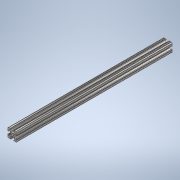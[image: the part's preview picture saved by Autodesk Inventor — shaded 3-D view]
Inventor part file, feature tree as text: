
AUTODESK INVENTOR PART (.ipt)
format: ipt  version: 2020 (Build 240168000, 168)  size: 239,104 bytes
history: native  units: in
note: dims shown in document units (in); Inventor stores cm internally (conversion verified against a paired STEP export)
features: extrude x1, sketch x1
ambient origin geometry x8: Origin, YZ Plane, XZ Plane, XY Plane, X Axis, Y Axis, Z Axis, Center Point
bodies: Solid1 (feature_tree)
feature tree (2):
  extrude  "Extrusion1"  [1 undecoded]
  sketch  "Sketch1"  dims[d0=17.0in d1=0.0in]
note: 1 required parameter value undecoded (feature->parameter linkage not recoverable at this tier; creation-order binding heuristic only, values carry confidence <= 0.55)
